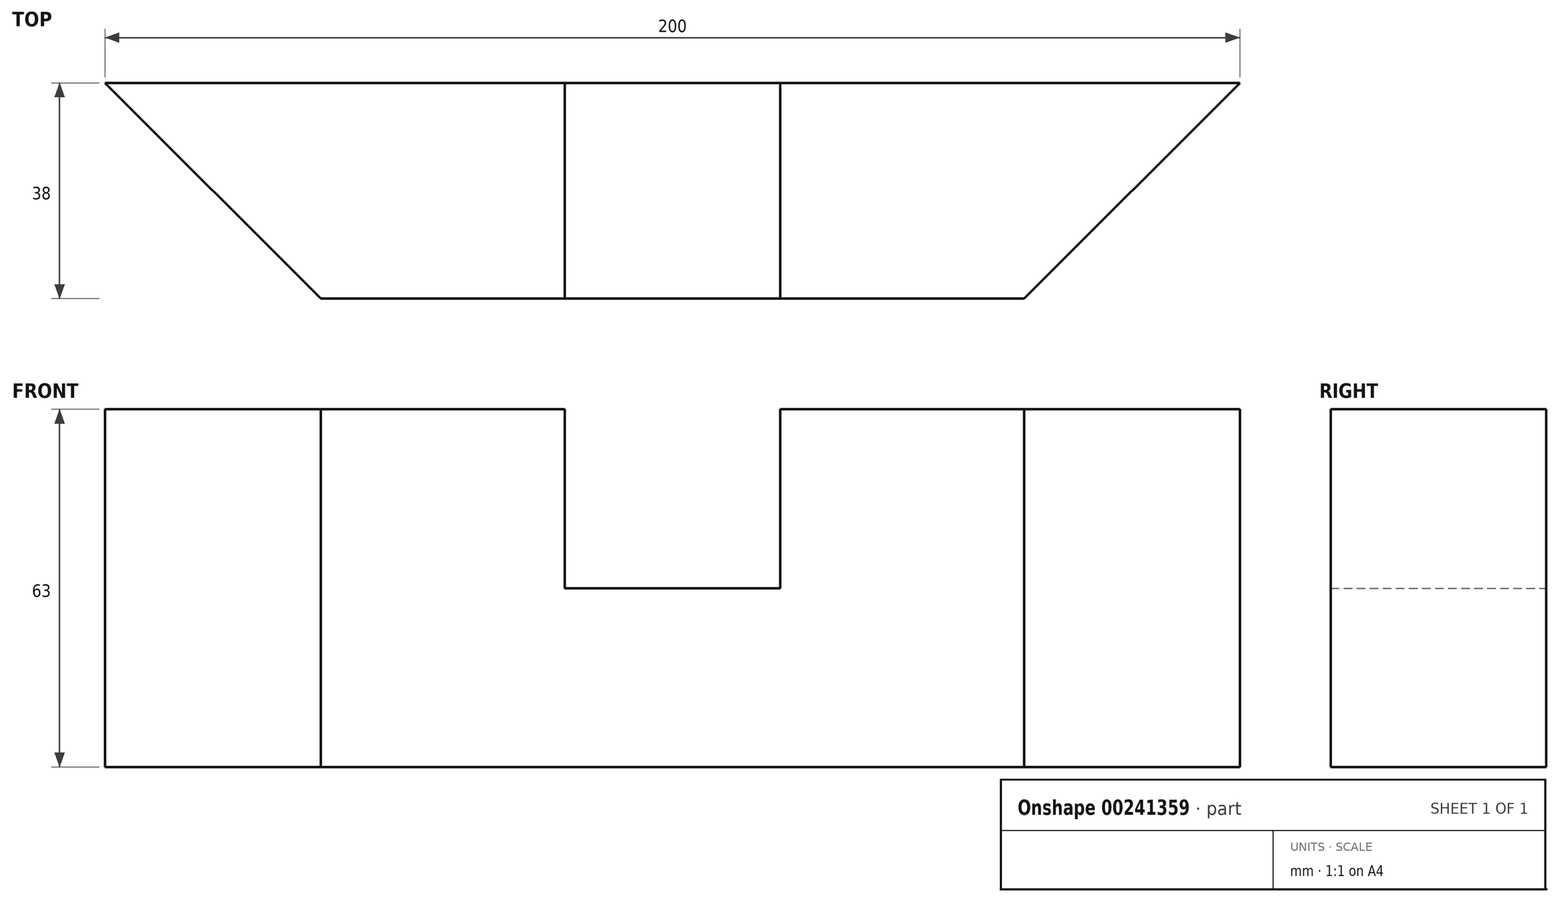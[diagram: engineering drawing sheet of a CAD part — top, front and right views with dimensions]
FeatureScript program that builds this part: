
annotation { "Feature Type Name" : "Feature", "Feature Type Description" : "" }
export const myFeature = defineFeature(function(context is Context, id is Id, definition is map)
    precondition{}
    {
        {
            var Q0;
            Q0=qCreatedBy(makeId("Top.planeOp"),FACE);
            var sketch = newSketch(context, id + "F0", { "sketchPlane" : qUnion([Q0])});
            skLineSegment(sketch, "E0", {"start": v(0, 0) * mm, "end": v(200, 0) * mm});
            skLineSegment(sketch, "E1", {"start": v(200, 0) * mm, "end": v(162, -38) * mm});
            skLineSegment(sketch, "E2", {"start": v(162, -38) * mm, "end": v(38, -38) * mm});
            skLineSegment(sketch, "E3", {"start": v(38, -38) * mm, "end": v(0, 0) * mm});
            skSolve(sketch);
        }
        {
            var Q0;
            Q0 = qSketchRegion(id + "F0", true);
            extrude(context, id + "F1", {"entities" : qUnion([Q0]), "depth" : 63 * mm});
        }
        {
            var Q0;
            Q0=makeQuery(id+"F1.opExtrude","SWEPT_FACE",FACE,{"disambiguationData":[OSD([sQuery(id+"F0.wireOp",EDGE,"E0")])]});
            var sketch = newSketch(context, id + "F2", { "sketchPlane" : qUnion([Q0])});
            skLineSegment(sketch, "E4.bottom", {"start": v(-81, 63) * mm, "end": v(-119, 63) * mm});
            skLineSegment(sketch, "E4.top", {"start": v(-81, 0) * mm, "end": v(-119, 0) * mm});
            skLineSegment(sketch, "E4.left", {"start": v(-81, 63) * mm, "end": v(-81, 0) * mm});
            skLineSegment(sketch, "E4.right", {"start": v(-119, 63) * mm, "end": v(-119, 0) * mm});
            skPoint(sketch, "E4.middle", {"position": v(-100, 31.5) * mm});
            skPoint(sketch, "E4.middle.positionSnap0", {"position": v(0, 31.5) * mm});
            skPoint(sketch, "E4.middle.positionSnap1", {"position": v(-100, 0) * mm});
            skPoint(sketch, "E4.centerSnap0", {"position": v(0, 31.5) * mm});
            skPoint(sketch, "E4.centerSnap1", {"position": v(-100, 0) * mm});
            skLineSegment(sketch, "E5", {"start": v(-119, 31.5) * mm, "end": v(-81, 31.5) * mm});
            skSolve(sketch);
        }
        {
            var Q0;
            {var subQ0=sQuery(id+"F2.wireOp",EDGE,"E4.bottom");Q0=makeQuery(id+"F2.imprint","IMPRINT",FACE,{"disambiguationData":[TD([[makeQuery(id+"F2.imprint","IMPRINT",EDGE,{"derivedFrom":subQ0}),1.0]])]});}
            extrude(context, id + "F3", {"entities" : qUnion([Q0]), "operationType" : NewBodyOperationType.REMOVE, "endBound" : BoundingType.THROUGH_ALL, "oppositeDirection" : true, "depth" : 25 * mm});
        }
    });
